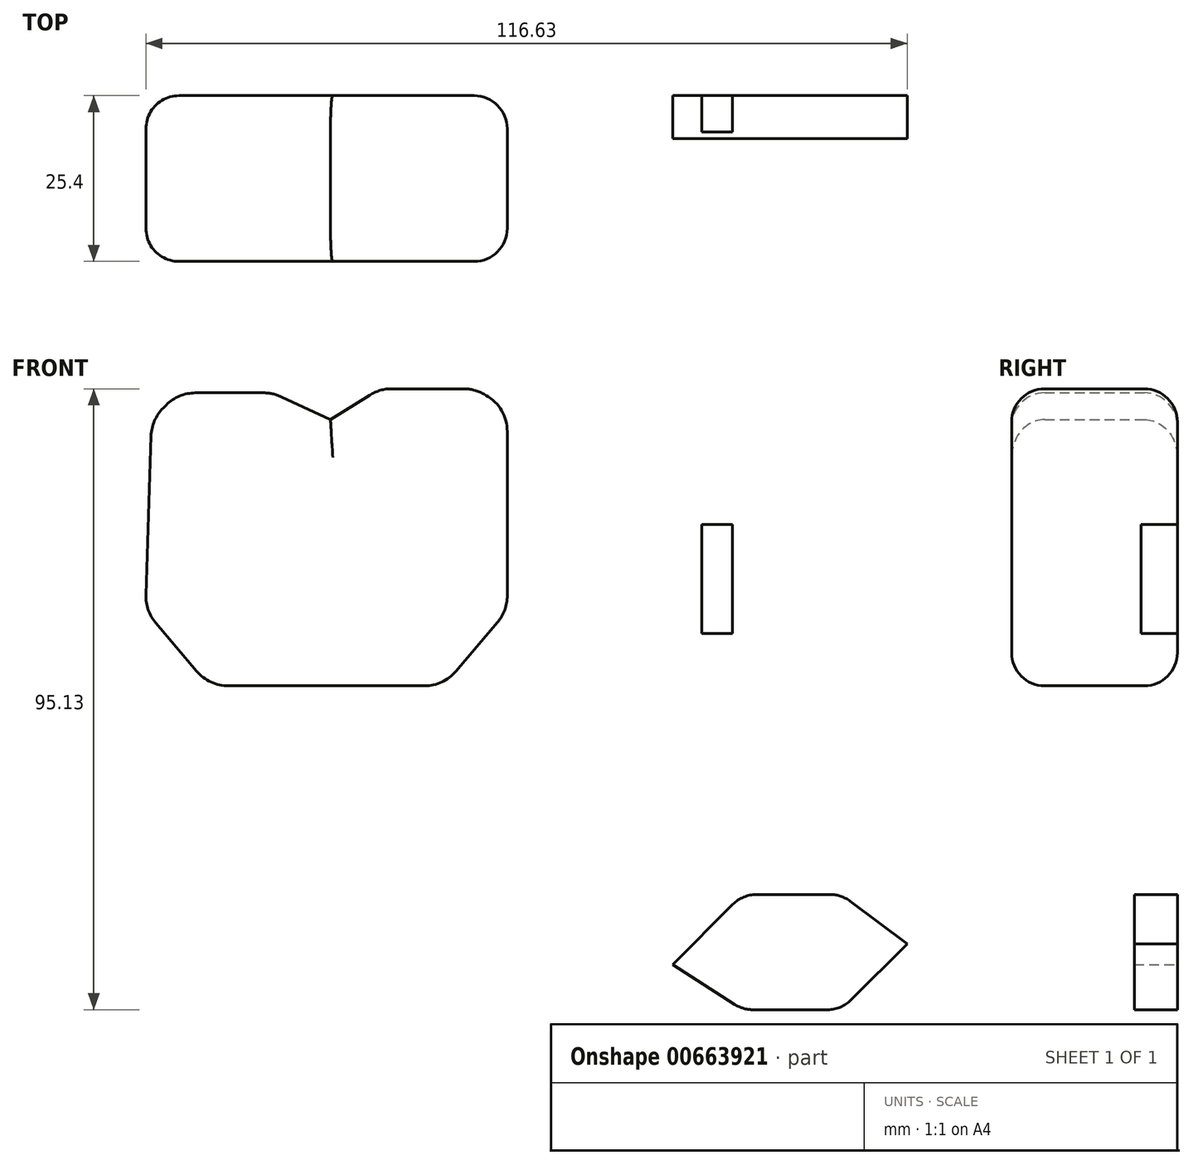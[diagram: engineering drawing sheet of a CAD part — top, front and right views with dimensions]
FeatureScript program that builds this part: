
annotation { "Feature Type Name" : "Feature", "Feature Type Description" : "" }
export const myFeature = defineFeature(function(context is Context, id is Id, definition is map)
    precondition{}
    {
        {
            var Q0;
            Q0=qCreatedBy(makeId("Front.planeOp"),FACE);
            var sketch = newSketch(context, id + "F0", { "sketchPlane" : qUnion([Q0])});
            skLineSegment(sketch, "E0", {"start": v(-37.8, 40.8) * mm, "end": v(-45.35, 44.3) * mm});
            skLineSegment(sketch, "E1", {"start": v(-37.8, 40.8) * mm, "end": v(-31.78, 44.55) * mm});
            skLineSegment(sketch, "E2", {"start": v(-48.02, 44.89) * mm, "end": v(-58.48, 44.89) * mm});
            skLineSegment(sketch, "E3", {"start": v(-28.42, 45.52) * mm, "end": v(-17.41, 45.52) * mm});
            skLineSegment(sketch, "E4", {"start": v(-62.97, 43.03) * mm, "end": v(-63.43, 42.57) * mm});
            skLineSegment(sketch, "E5", {"start": v(-14.3, 44.7) * mm, "end": v(-13.95, 44.5) * mm});
            skLineSegment(sketch, "E6", {"start": v(-10.71, 38.97) * mm, "end": v(-10.71, 13.83) * mm});
            skLineSegment(sketch, "E7", {"start": v(-12.22, 9.72) * mm, "end": v(-18.57, 2.24) * mm});
            skLineSegment(sketch, "E8", {"start": v(-23.41, 0) * mm, "end": v(-53.45, 0) * mm});
            skLineSegment(sketch, "E9", {"start": v(-58.29, 2.24) * mm, "end": v(-64.56, 9.63) * mm});
            skLineSegment(sketch, "E10", {"start": v(-66.07, 13.95) * mm, "end": v(-65.29, 38.28) * mm});
            skPoint(sketch, "E11.visualSharp", {"position": v(-46.62, 44.89) * mm});
            skArc(sketch, "E11.filletArc", {"start": v(-45.35, 44.3) * mm, "mid": v(-46.65, 44.74) * mm, "end": v(-48.02, 44.89) * mm});
            skPoint(sketch, "E12.visualSharp", {"position": v(-61.11, 44.89) * mm});
            skArc(sketch, "E12.filletArc", {"start": v(-58.48, 44.89) * mm, "mid": v(-60.9, 44.4) * mm, "end": v(-62.97, 43.03) * mm});
            skPoint(sketch, "E13.visualSharp", {"position": v(-65.2, 40.8) * mm});
            skArc(sketch, "E13.filletArc", {"start": v(-63.43, 42.57) * mm, "mid": v(-64.77, 40.6) * mm, "end": v(-65.29, 38.28) * mm});
            skPoint(sketch, "E14.visualSharp", {"position": v(-66.15, 11.5) * mm});
            skArc(sketch, "E14.filletArc", {"start": v(-66.07, 13.95) * mm, "mid": v(-65.72, 11.65) * mm, "end": v(-64.56, 9.63) * mm});
            skPoint(sketch, "E15.visualSharp", {"position": v(-56.38, 0) * mm});
            skArc(sketch, "E15.filletArc", {"start": v(-58.29, 2.24) * mm, "mid": v(-56.11, 0.59) * mm, "end": v(-53.45, 0) * mm});
            skPoint(sketch, "E16.visualSharp", {"position": v(-20.48, 0) * mm});
            skArc(sketch, "E16.filletArc", {"start": v(-23.41, 0) * mm, "mid": v(-20.75, 0.59) * mm, "end": v(-18.57, 2.24) * mm});
            skPoint(sketch, "E17.visualSharp", {"position": v(-10.71, 11.5) * mm});
            skArc(sketch, "E17.filletArc", {"start": v(-12.22, 9.72) * mm, "mid": v(-11.1, 11.64) * mm, "end": v(-10.71, 13.83) * mm});
            skPoint(sketch, "E18.visualSharp", {"position": v(-10.71, 42.68) * mm});
            skArc(sketch, "E18.filletArc", {"start": v(-10.71, 38.97) * mm, "mid": v(-11.58, 42.17) * mm, "end": v(-13.95, 44.5) * mm});
            skPoint(sketch, "E19.visualSharp", {"position": v(-15.75, 45.52) * mm});
            skArc(sketch, "E19.filletArc", {"start": v(-14.3, 44.7) * mm, "mid": v(-15.8, 45.31) * mm, "end": v(-17.41, 45.52) * mm});
            skPoint(sketch, "E20.visualSharp", {"position": v(-30.24, 45.52) * mm});
            skArc(sketch, "E20.filletArc", {"start": v(-28.42, 45.52) * mm, "mid": v(-30.17, 45.27) * mm, "end": v(-31.78, 44.55) * mm});
            skSolve(sketch);
        }
        {
            var Q0;
            Q0 = qSketchRegion(id + "F0", true);
            extrude(context, id + "F1", {"entities" : qUnion([Q0]), "depth" : 25.4 * mm, "offsetDistance" : 25.4 * mm});
        }
        {
            var Q0;
            Q0=makeQuery(id+"F1.opExtrude","CAP_EDGE",EDGE,{"disambiguationData":[OSD([sQuery(id+"F0.wireOp",EDGE,"E12.filletArc")])],"isStart":false});
            var Q1;
            Q1=makeQuery(id+"F1.opExtrude","CAP_EDGE",EDGE,{"disambiguationData":[OSD([sQuery(id+"F0.wireOp",EDGE,"E19.filletArc")])],"isStart":true});
            var Q2;
            Q2=makeQuery(id+"F1.opExtrude","SWEPT_FACE",FACE,{"disambiguationData":[OSD([sQuery(id+"F0.wireOp",EDGE,"E6")])]});
            var Q3;
            Q3=makeQuery(id+"F1.opExtrude","SWEPT_FACE",FACE,{"disambiguationData":[OSD([sQuery(id+"F0.wireOp",EDGE,"E10")])]});
            var Q4;
            Q4=makeQuery(id+"F1.opExtrude","SWEPT_EDGE",EDGE,{"disambiguationData":[OSD([sQuery(id+"F0.wireOp",EDGE,"E5"),sQuery(id+"F0.wireOp",EDGE,"E18.filletArc")])]});
            var Q5;
            Q5=makeQuery(id+"F1.opExtrude","SWEPT_EDGE",EDGE,{"disambiguationData":[OSD([sQuery(id+"F0.wireOp",EDGE,"E4"),sQuery(id+"F0.wireOp",EDGE,"E13.filletArc")])]});
            fillet(context, id + "F2", {"entities" : qUnion([Q0, Q1, Q2, Q3, Q4, Q5]), "radius" : 5.08 * mm, "tangentPropagation" : true, "allowEdgeOverflow" : false});
        }
        {
            var Q0;
            Q0=qCreatedBy(makeId("Front.planeOp"),FACE);
            var sketch = newSketch(context, id + "F3", { "sketchPlane" : qUnion([Q0])});
            skLineSegment(sketch, "E21.bottom", {"start": v(19.06, 8.03) * mm, "end": v(23.78, 8.03) * mm});
            skLineSegment(sketch, "E21.top", {"start": v(19.06, 24.73) * mm, "end": v(23.78, 24.73) * mm});
            skLineSegment(sketch, "E21.left", {"start": v(19.06, 8.03) * mm, "end": v(19.06, 24.73) * mm});
            skLineSegment(sketch, "E21.right", {"start": v(23.78, 8.03) * mm, "end": v(23.78, 24.73) * mm});
            skSolve(sketch);
        }
        {
            var Q0;
            Q0 = qSketchRegion(id + "F3", true);
            extrude(context, id + "F4", {"entities" : qUnion([Q0]), "depth" : 5.6 * mm, "offsetDistance" : 25.4 * mm});
        }
        {
            var Q0;
            Q0=qCreatedBy(makeId("Front.planeOp"),FACE);
            var sketch = newSketch(context, id + "F5", { "sketchPlane" : qUnion([Q0])});
            skLineSegment(sketch, "E22", {"start": v(14.65, -42.68) * mm, "end": v(25.36, -31.97) * mm});
            skLineSegment(sketch, "E23", {"start": v(14.65, -42.68) * mm, "end": v(25.36, -49.61) * mm});
            skLineSegment(sketch, "E24", {"start": v(25.36, -31.97) * mm, "end": v(40.48, -31.97) * mm});
            skLineSegment(sketch, "E25", {"start": v(25.36, -49.61) * mm, "end": v(40.48, -49.61) * mm});
            skLineSegment(sketch, "E26", {"start": v(40.48, -31.97) * mm, "end": v(50.56, -39.53) * mm});
            skLineSegment(sketch, "E27", {"start": v(40.48, -49.61) * mm, "end": v(50.56, -39.53) * mm});
            skSolve(sketch);
        }
        {
            var Q0;
            Q0=makeQuery(id+"F5.imprint","IMPRINT",FACE,{"disambiguationData":[TD([[makeQuery(id+"F5.imprint","IMPRINT",EDGE,{"derivedFrom":sQuery(id+"F5.wireOp",EDGE,"E22")}),-1.0]])]});
            extrude(context, id + "F6", {"entities" : qUnion([Q0]), "depth" : 6.6 * mm, "offsetDistance" : 25.4 * mm});
        }
        {
            var Q0;
            Q0=makeQuery(id+"F6.opExtrude","SWEPT_EDGE",EDGE,{"disambiguationData":[OSD([sQuery(id+"F5.wireOp",EDGE,"E24"),sQuery(id+"F5.wireOp",EDGE,"E26")])]});
            var Q1;
            Q1=makeQuery(id+"F6.opExtrude","SWEPT_EDGE",EDGE,{"disambiguationData":[OSD([sQuery(id+"F5.wireOp",EDGE,"E25"),sQuery(id+"F5.wireOp",EDGE,"E27")])]});
            var Q2;
            Q2=makeQuery(id+"F6.opExtrude","SWEPT_EDGE",EDGE,{"disambiguationData":[OSD([sQuery(id+"F5.wireOp",EDGE,"E23"),sQuery(id+"F5.wireOp",EDGE,"E25")])]});
            var Q3;
            Q3=makeQuery(id+"F6.opExtrude","SWEPT_EDGE",EDGE,{"disambiguationData":[OSD([sQuery(id+"F5.wireOp",EDGE,"E22"),sQuery(id+"F5.wireOp",EDGE,"E24")])]});
            fillet(context, id + "F7", {"entities" : qUnion([Q0, Q1, Q2, Q3]), "radius" : 5.08 * mm, "tangentPropagation" : true, "allowEdgeOverflow" : false});
        }
    });
